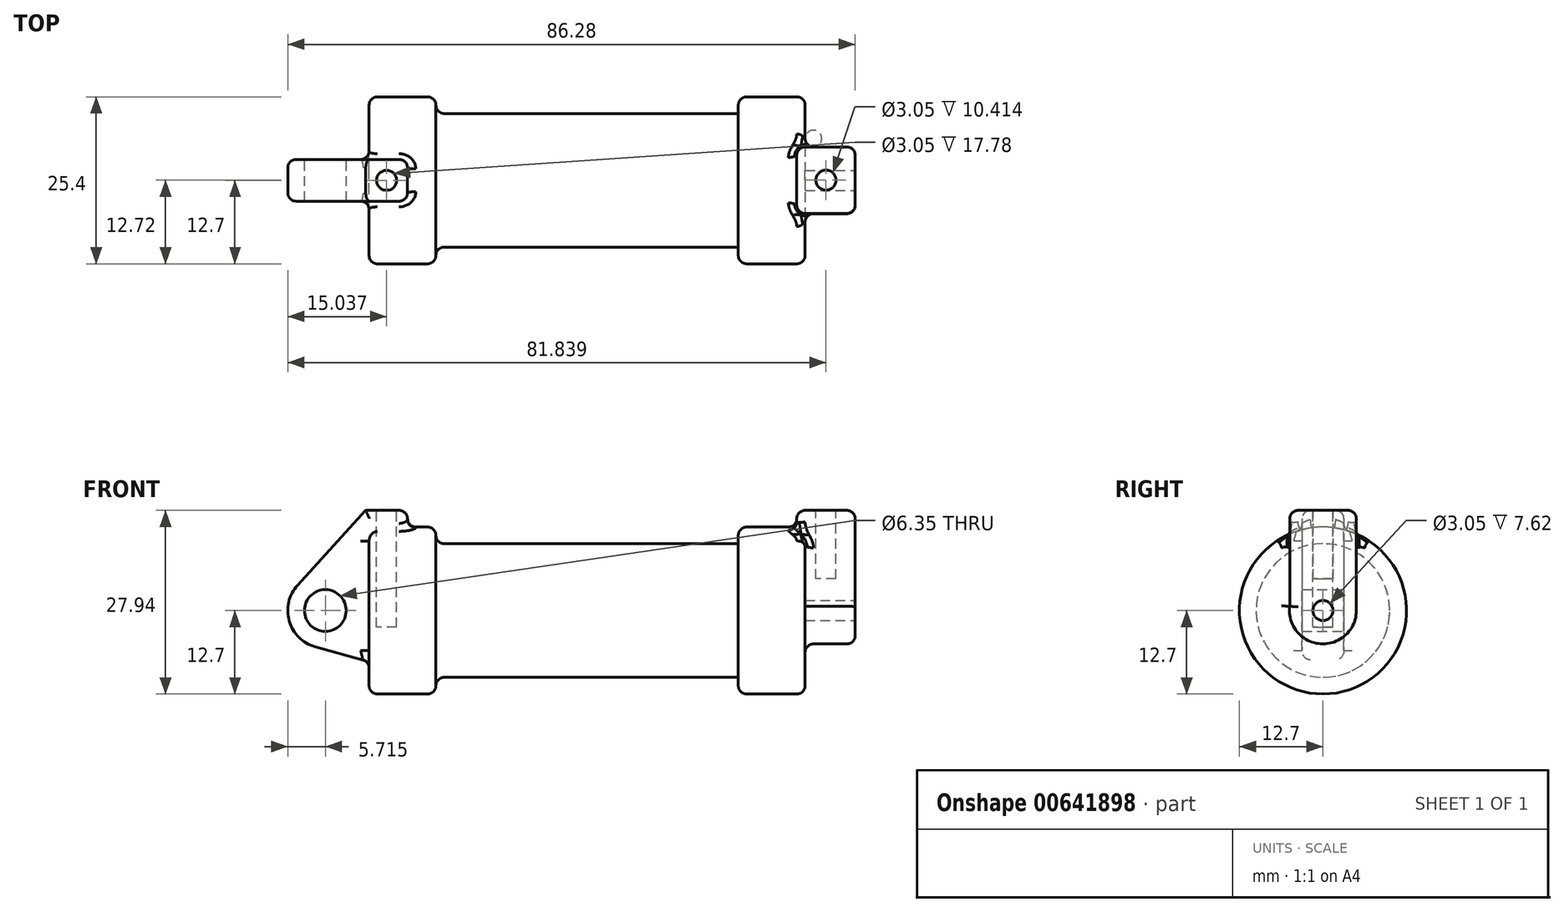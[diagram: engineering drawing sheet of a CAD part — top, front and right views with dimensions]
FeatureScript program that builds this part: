
annotation { "Feature Type Name" : "Feature", "Feature Type Description" : "" }
export const myFeature = defineFeature(function(context is Context, id is Id, definition is map)
    precondition{}
    {
        {
            var Q0;
            Q0=qCreatedBy(makeId("Front.planeOp"),FACE);
            var sketch = newSketch(context, id + "F0", { "sketchPlane" : qUnion([Q0])});
            skLineSegment(sketch, "E0", {"start": v(0, 0) * mm, "end": v(0, 12.7) * mm});
            skLineSegment(sketch, "E1", {"start": v(0, 12.7) * mm, "end": v(10.16, 12.7) * mm});
            skLineSegment(sketch, "E2", {"start": v(10.16, 12.7) * mm, "end": v(10.16, 10.16) * mm});
            skLineSegment(sketch, "E3", {"start": v(10.16, 10.16) * mm, "end": v(56.13, 10.16) * mm});
            skLineSegment(sketch, "E4", {"start": v(56.13, 10.16) * mm, "end": v(56.13, 12.7) * mm});
            skLineSegment(sketch, "E5", {"start": v(56.13, 12.7) * mm, "end": v(66.3, 12.7) * mm});
            skLineSegment(sketch, "E6", {"start": v(66.3, 12.7) * mm, "end": v(66.3, 0) * mm});
            skLineSegment(sketch, "E7", {"start": v(66.3, 0) * mm, "end": v(0, 0) * mm});
            skLineSegment(sketch, "E8", {"start": v(5.84, 15.24) * mm, "end": v(-0.5, 15.24) * mm});
            skLineSegment(sketch, "E9", {"start": v(-0.5, 15.24) * mm, "end": v(-10.88, 3.85) * mm});
            skLineSegment(sketch, "E10", {"start": v(0, 0) * mm, "end": v(-6.65, 0) * mm});
            skCircle(sketch, "E11", {"center": v(-6.65, 0) * mm, "radius": 5.72 * mm});
            skCircle(sketch, "E12", {"center": v(-6.65, 0) * mm, "radius": 3.18 * mm});
            skLineSegment(sketch, "E13", {"start": v(5.84, 15.24) * mm, "end": v(5.84, -9.4) * mm});
            skLineSegment(sketch, "E14", {"start": v(5.84, -9.4) * mm, "end": v(-8.18, -5.5) * mm});
            skSolve(sketch);
        }
        {
            var Q0;
            {var subQ0=sQuery(id+"F0.wireOp",EDGE,"E2");Q0=makeQuery(id+"F0.imprint","IMPRINT",FACE,{"disambiguationData":[TD([[makeQuery(id+"F0.imprint","IMPRINT",EDGE,{"derivedFrom":subQ0}),-1.0]])]});}
            var Q1;
            {var subQ0=sQuery(id+"F0.wireOp",EDGE,"E0");Q1=makeQuery(id+"F0.imprint","IMPRINT",FACE,{"disambiguationData":[TD([[makeQuery(id+"F0.imprint","IMPRINT",EDGE,{"derivedFrom":subQ0}),-1.0]])]});}
            var Q2;
            Q2=sQuery(id+"F0.wireOp",EDGE,"E7");
            revolve(context, id + "F1", {"entities" : qUnion([Q0, Q1]), "axis" : qUnion([Q2]), "revolveType" : RevolveType.FULL});
        }
        {
            var Q0;
            {var subQ1=sQuery(id+"F0.wireOp",EDGE,"E0");Q0=makeQuery(id+"F0.imprint","IMPRINT",FACE,{"disambiguationData":[TD([[makeQuery(id+"F0.imprint","IMPRINT",EDGE,{"derivedFrom":subQ1}),1.0]])]});}
            var Q1;
            {var subQ0=sQuery(id+"F0.wireOp",EDGE,"E0");Q1=makeQuery(id+"F0.imprint","IMPRINT",FACE,{"disambiguationData":[TD([[makeQuery(id+"F0.imprint","IMPRINT",EDGE,{"derivedFrom":subQ0}),-1.0]])]});}
            var Q2;
            {var subQ0=sQuery(id+"F0.wireOp",EDGE,"E14");Q2=makeQuery(id+"F0.imprint","IMPRINT",FACE,{"disambiguationData":[TD([[makeQuery(id+"F0.imprint","IMPRINT",EDGE,{"derivedFrom":subQ0}),-1.0]])]});}
            var Q3;
            {var subQ5=sQuery(id+"F0.wireOp",EDGE,"E12");Q3=makeQuery(id+"F0.imprint","IMPRINT",FACE,{"disambiguationData":[TD([[makeQuery(id+"F0.imprint","IMPRINT",EDGE,{"derivedFrom":subQ5}),-1.0]])]});}
            extrude(context, id + "F2", {"entities" : qUnion([Q0, Q1, Q2, Q3]), "operationType" : NewBodyOperationType.ADD, "endBound" : BoundingType.SYMMETRIC, "depth" : 6.35 * mm, "offsetDistance" : 25.4 * mm});
        }
        {
            var Q0;
            Q0=makeQuery(id+"F1.opRevolve","SWEPT_FACE",FACE,{"disambiguationData":[OSD([sQuery(id+"F0.wireOp",EDGE,"E6")])]});
            var sketch = newSketch(context, id + "F3", { "sketchPlane" : qUnion([Q0])});
            skCircle(sketch, "E15", {"center": v(0, 0) * mm, "radius": 1.52 * mm});
            skCircle(sketch, "E16", {"center": v(0, 0) * mm, "radius": 5.08 * mm});
            skLineSegment(sketch, "E17.top", {"start": v(5.08, 15.24) * mm, "end": v(-5.04, 15.24) * mm});
            skLineSegment(sketch, "E17.left", {"start": v(5.08, 0) * mm, "end": v(5.08, 15.24) * mm});
            skLineSegment(sketch, "E17.right", {"start": v(-5.04, -0.01) * mm, "end": v(-5.04, 15.24) * mm});
            skSolve(sketch);
        }
        {
            var Q0;
            Q0 = qSketchRegion(id + "F3", true);
            extrude(context, id + "F4", {"entities" : qUnion([Q0]), "operationType" : NewBodyOperationType.ADD, "oppositeDirection" : true, "depth" : 1.27 * mm, "offsetDistance" : 25.4 * mm, "hasSecondDirection" : true, "secondDirectionOppositeDirection" : false, "secondDirectionDepth" : 7.62 * mm});
        }
        {
            var Q0;
            Q0=makeQuery(id+"F4.opExtrude","SWEPT_FACE",FACE,{"disambiguationData":[OSD([sQuery(id+"F3.wireOp",EDGE,"E17.top")])]});
            var sketch = newSketch(context, id + "F5", { "sketchPlane" : qUnion([Q0])});
            skCircle(sketch, "E18", {"center": v(69.47, 0.02) * mm, "radius": 1.52 * mm});
            skPoint(sketch, "E18.centerSnap0", {"position": v(69.47, 5.08) * mm});
            skPoint(sketch, "E18.centerSnap1", {"position": v(65.02, 0.02) * mm});
            skSolve(sketch);
        }
        {
            var Q0;
            Q0 = qSketchRegion(id + "F5", true);
            extrude(context, id + "F6", {"entities" : qUnion([Q0]), "operationType" : NewBodyOperationType.REMOVE, "oppositeDirection" : true, "depth" : 10.4 * mm, "offsetDistance" : 25.4 * mm});
        }
        {
            var Q0;
            Q0=makeQuery(id+"F2.opExtrude","SWEPT_FACE",FACE,{"disambiguationData":[OSD([sQuery(id+"F0.wireOp",EDGE,"E8")])]});
            var sketch = newSketch(context, id + "F7", { "sketchPlane" : qUnion([Q0])});
            skCircle(sketch, "E19", {"center": v(2.67, 0) * mm, "radius": 1.52 * mm});
            skPoint(sketch, "E19.centerSnap0", {"position": v(2.67, 3.18) * mm});
            skPoint(sketch, "E19.centerSnap1", {"position": v(5.84, 0) * mm});
            skSolve(sketch);
        }
        {
            var Q0;
            Q0=makeQuery(id+"F7.imprint","IMPRINT",FACE,{"disambiguationData":[TD([[makeQuery(id+"F7.imprint","IMPRINT",EDGE,{"derivedFrom":sQuery(id+"F7.wireOp",EDGE,"E19")}),1.0]])]});
            extrude(context, id + "F8", {"entities" : qUnion([Q0]), "operationType" : NewBodyOperationType.REMOVE, "oppositeDirection" : true, "depth" : 17.78 * mm, "offsetDistance" : 25.4 * mm});
        }
        {
            var Q0;
            Q0=makeQuery(id+"F1.opRevolve","SWEPT_EDGE",EDGE,{"disambiguationData":[OSD([sQuery(id+"F0.wireOp",EDGE,"E1"),sQuery(id+"F0.wireOp",EDGE,"E2")])]});
            var Q1;
            Q1=makeQuery(id+"F1.opRevolve","SWEPT_EDGE",EDGE,{"disambiguationData":[OSD([sQuery(id+"F0.wireOp",EDGE,"E2"),sQuery(id+"F0.wireOp",EDGE,"E3")])]});
            var Q2;
            Q2=makeQuery(id+"F2.opExtrude","CAP_EDGE",EDGE,{"disambiguationData":[OSD([sQuery(id+"F0.wireOp",EDGE,"E8")])],"isStart":false});
            var Q3;
            Q3=makeQuery(id+"F2.opExtrude","SWEPT_EDGE",EDGE,{"disambiguationData":[OSD([sQuery(id+"F0.wireOp",EDGE,"E8"),sQuery(id+"F0.wireOp",EDGE,"E13")])]});
            var Q4;
            Q4=makeQuery(id+"F2.opExtrude","CAP_EDGE",EDGE,{"disambiguationData":[OSD([sQuery(id+"F0.wireOp",EDGE,"E8")])],"isStart":true});
            var Q5;
            Q5=makeQuery(id+"F2.boolean.opBoolean","INTERSECT",EDGE,{"derivedFrom":[makeQuery(id+"F1.opRevolve","SWEPT_FACE",FACE,{"disambiguationData":[OSD([sQuery(id+"F0.wireOp",EDGE,"E1")])]}),makeQuery(id+"F2.opExtrude","SWEPT_FACE",FACE,{"disambiguationData":[OSD([sQuery(id+"F0.wireOp",EDGE,"E13")])]})]});
            var Q6;
            Q6=makeQuery(id+"F2.opExtrude","CAP_EDGE",EDGE,{"disambiguationData":[OSD([sQuery(id+"F0.wireOp",EDGE,"E13")])],"isStart":false});
            var Q7;
            Q7=makeQuery(id+"F2.opExtrude","CAP_EDGE",EDGE,{"disambiguationData":[OSD([sQuery(id+"F0.wireOp",EDGE,"E13")])],"isStart":true});
            var Q8;
            Q8=makeQuery(id+"F1.opRevolve","SWEPT_EDGE",EDGE,{"disambiguationData":[OSD([sQuery(id+"F0.wireOp",EDGE,"E5"),sQuery(id+"F0.wireOp",EDGE,"E6")])]});
            var Q9;
            Q9=makeQuery(id+"F1.opRevolve","SWEPT_FACE",FACE,{"disambiguationData":[OSD([sQuery(id+"F0.wireOp",EDGE,"E5")])]});
            var Q10;
            Q10=makeQuery(id+"F4.opExtrude","CAP_EDGE",EDGE,{"disambiguationData":[OSD([sQuery(id+"F3.wireOp",EDGE,"E17.right")])],"isStart":true});
            var Q11;
            Q11=makeQuery(id+"F4.opExtrude","SWEPT_EDGE",EDGE,{"disambiguationData":[OSD([sQuery(id+"F3.wireOp",EDGE,"E17.top"),sQuery(id+"F3.wireOp",EDGE,"E17.right")])]});
            var Q12;
            Q12=makeQuery(id+"F4.opExtrude","CAP_EDGE",EDGE,{"disambiguationData":[OSD([sQuery(id+"F3.wireOp",EDGE,"E17.top")])],"isStart":true});
            var Q13;
            Q13=makeQuery(id+"F4.opExtrude","SWEPT_EDGE",EDGE,{"disambiguationData":[OSD([sQuery(id+"F3.wireOp",EDGE,"E17.top"),sQuery(id+"F3.wireOp",EDGE,"E17.left")])]});
            var Q14;
            Q14=makeQuery(id+"F4.opExtrude","CAP_EDGE",EDGE,{"disambiguationData":[OSD([sQuery(id+"F3.wireOp",EDGE,"E17.top")])],"isStart":false});
            var Q15;
            Q15=makeQuery(id+"F1.opRevolve","SWEPT_EDGE",EDGE,{"disambiguationData":[OSD([sQuery(id+"F0.wireOp",EDGE,"E0"),sQuery(id+"F0.wireOp",EDGE,"E1")])]});
            var Q16;
            Q16=makeQuery(id+"F2.opExtrude","CAP_EDGE",EDGE,{"disambiguationData":[OSD([sQuery(id+"F0.wireOp",EDGE,"E9")])],"isStart":true});
            var Q17;
            Q17=makeQuery(id+"F4.opExtrude","CAP_EDGE",EDGE,{"disambiguationData":[OSD([sQuery(id+"F3.wireOp",EDGE,"E17.left")])],"isStart":true});
            var Q18;
            Q18=makeQuery(id+"F2.opExtrude","CAP_EDGE",EDGE,{"disambiguationData":[OSD([sQuery(id+"F0.wireOp",EDGE,"E9")])],"isStart":false});
            var Q19;
            Q19=makeQuery(id+"F2.opExtrude","CAP_EDGE",EDGE,{"disambiguationData":[OSD([sQuery(id+"F0.wireOp",EDGE,"E11")])],"isStart":false});
            var Q20;
            Q20=makeQuery(id+"F2.opExtrude","CAP_EDGE",EDGE,{"disambiguationData":[OSD([sQuery(id+"F0.wireOp",EDGE,"E14")])],"isStart":false});
            var Q21;
            Q21=makeQuery(id+"F2.boolean.opBoolean","INTERSECT",EDGE,{"derivedFrom":[makeQuery(id+"F1.opRevolve","SWEPT_FACE",FACE,{"disambiguationData":[OSD([sQuery(id+"F0.wireOp",EDGE,"E0")])]}),makeQuery(id+"F2.opExtrude","CAP_FACE",FACE,{"disambiguationData":[OSD([sQuery(id+"F0.wireOp",EDGE,"E8"),sQuery(id+"F0.wireOp",EDGE,"E9"),sQuery(id+"F0.wireOp",EDGE,"E11"),sQuery(id+"F0.wireOp",EDGE,"E12"),sQuery(id+"F0.wireOp",EDGE,"E13"),sQuery(id+"F0.wireOp",EDGE,"E14")])],"isStart":false})]});
            var Q22;
            Q22=makeQuery(id+"F1.opRevolve","SWEPT_FACE",FACE,{"disambiguationData":[OSD([sQuery(id+"F0.wireOp",EDGE,"E0")])]});
            var Q23;
            Q23=makeQuery(id+"F2.opExtrude","CAP_EDGE",EDGE,{"disambiguationData":[OSD([sQuery(id+"F0.wireOp",EDGE,"E14")])],"isStart":true});
            var Q24;
            Q24=makeQuery(id+"F2.opExtrude","CAP_EDGE",EDGE,{"disambiguationData":[OSD([sQuery(id+"F0.wireOp",EDGE,"E11")])],"isStart":true});
            var Q25;
            Q25=makeQuery(id+"F4.boolean.opBoolean","INTERSECT",EDGE,{"derivedFrom":[makeQuery(id+"F1.opRevolve","SWEPT_FACE",FACE,{"disambiguationData":[OSD([sQuery(id+"F0.wireOp",EDGE,"E6")])]}),makeQuery(id+"F4.opExtrude","SWEPT_FACE",FACE,{"disambiguationData":[OSD([sQuery(id+"F3.wireOp",EDGE,"E16")])]})]});
            var Q26;
            Q26=makeQuery(id+"F4.opExtrude","CAP_EDGE",EDGE,{"disambiguationData":[OSD([sQuery(id+"F3.wireOp",EDGE,"E16")])],"isStart":true});
            var Q27;
            Q27=makeQuery(id+"F4.boolean.opBoolean","INTERSECT",EDGE,{"derivedFrom":[makeQuery(id+"F1.opRevolve","SWEPT_FACE",FACE,{"disambiguationData":[OSD([sQuery(id+"F0.wireOp",EDGE,"E6")])]}),makeQuery(id+"F4.opExtrude","SWEPT_FACE",FACE,{"disambiguationData":[OSD([sQuery(id+"F3.wireOp",EDGE,"E17.left")])]})]});
            var Q28;
            Q28=makeQuery(id+"F4.opExtrude","CAP_EDGE",EDGE,{"disambiguationData":[OSD([sQuery(id+"F3.wireOp",EDGE,"E17.left")])],"isStart":false});
            var Q29;
            Q29=makeQuery(id+"F2.boolean.opBoolean","INTERSECT",EDGE,{"derivedFrom":[makeQuery(id+"F1.opRevolve","SWEPT_FACE",FACE,{"disambiguationData":[OSD([sQuery(id+"F0.wireOp",EDGE,"E1")])]}),makeQuery(id+"F2.opExtrude","CAP_FACE",FACE,{"disambiguationData":[OSD([sQuery(id+"F0.wireOp",EDGE,"E8"),sQuery(id+"F0.wireOp",EDGE,"E9"),sQuery(id+"F0.wireOp",EDGE,"E11"),sQuery(id+"F0.wireOp",EDGE,"E12"),sQuery(id+"F0.wireOp",EDGE,"E13"),sQuery(id+"F0.wireOp",EDGE,"E14")])],"isStart":true})]});
            var Q30;
            Q30=makeQuery(id+"F4.boolean.opBoolean","INTERSECT",EDGE,{"derivedFrom":[makeQuery(id+"F1.opRevolve","SWEPT_FACE",FACE,{"disambiguationData":[OSD([sQuery(id+"F0.wireOp",EDGE,"E6")])]}),makeQuery(id+"F4.opExtrude","SWEPT_FACE",FACE,{"disambiguationData":[OSD([sQuery(id+"F3.wireOp",EDGE,"E17.right")])]})]});
            var Q31;
            Q31=makeQuery(id+"F4.opExtrude","CAP_EDGE",EDGE,{"disambiguationData":[OSD([sQuery(id+"F3.wireOp",EDGE,"E17.right")])],"isStart":false});
            var Q32;
            Q32=makeQuery(id+"F2.boolean.opBoolean","INTERSECT",EDGE,{"derivedFrom":[makeQuery(id+"F1.opRevolve","SWEPT_FACE",FACE,{"disambiguationData":[OSD([sQuery(id+"F0.wireOp",EDGE,"E1")])]}),makeQuery(id+"F2.opExtrude","CAP_FACE",FACE,{"disambiguationData":[OSD([sQuery(id+"F0.wireOp",EDGE,"E8"),sQuery(id+"F0.wireOp",EDGE,"E9"),sQuery(id+"F0.wireOp",EDGE,"E11"),sQuery(id+"F0.wireOp",EDGE,"E12"),sQuery(id+"F0.wireOp",EDGE,"E13"),sQuery(id+"F0.wireOp",EDGE,"E14")])],"isStart":false})]});
            fillet(context, id + "F9", {"entities" : qUnion([Q0, Q1, Q2, Q3, Q4, Q5, Q6, Q7, Q8, Q9, Q10, Q11, Q12, Q13, Q14, Q15, Q16, Q17, Q18, Q19, Q20, Q21, Q22, Q23, Q24, Q25, Q26, Q27, Q28, Q29, Q30, Q31, Q32]), "radius" : 1.27 * mm, "tangentPropagation" : true, "allowEdgeOverflow" : false});
        }
    });
